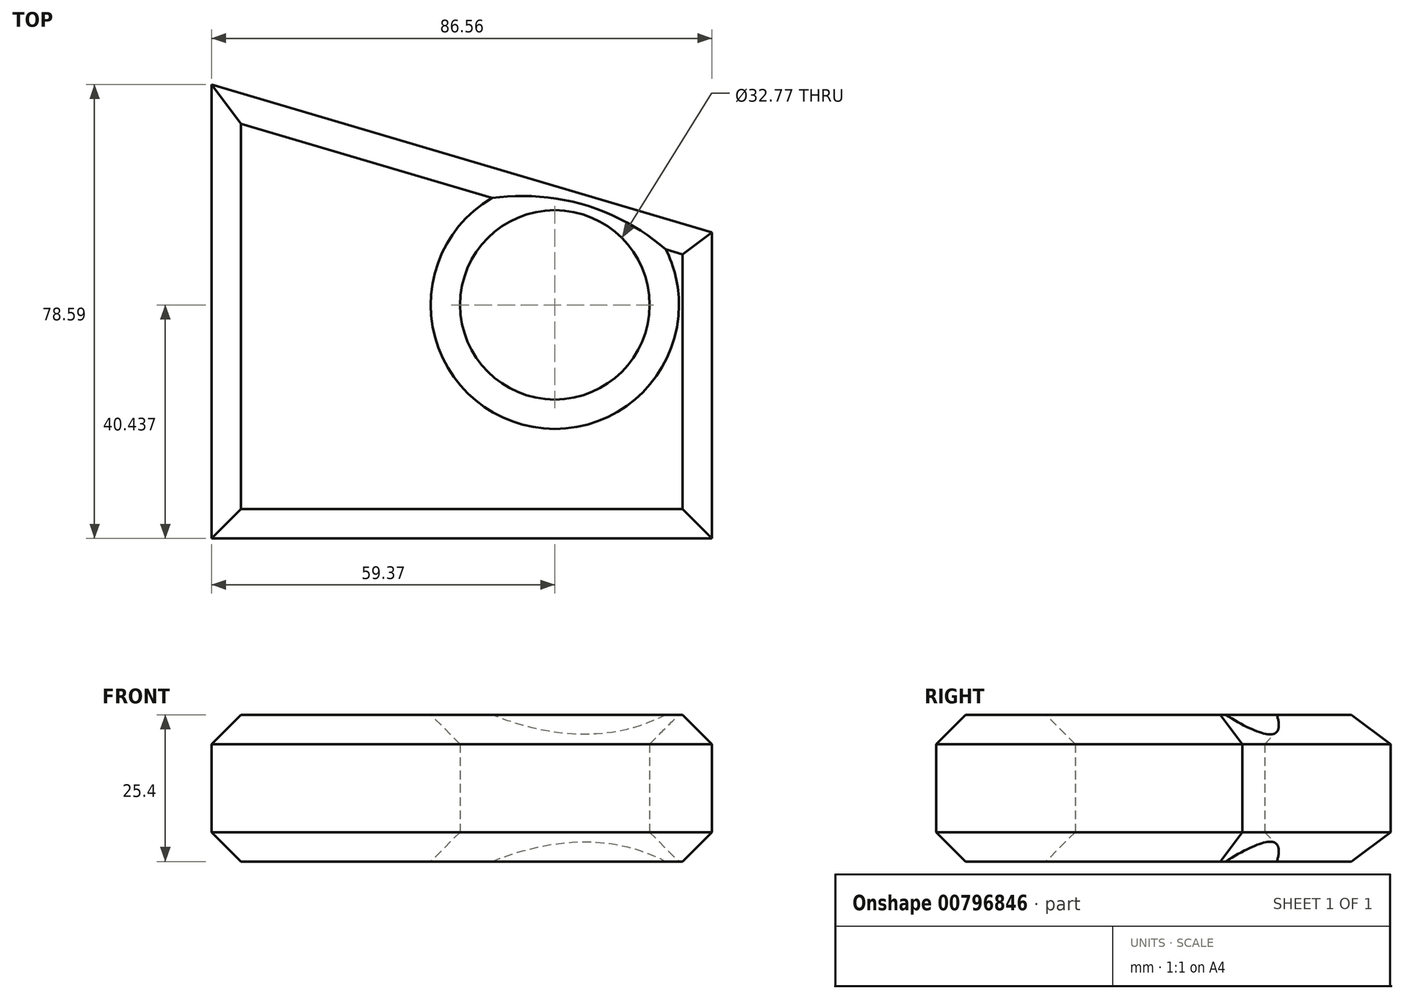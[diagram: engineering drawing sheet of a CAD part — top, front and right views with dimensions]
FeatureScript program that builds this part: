
annotation { "Feature Type Name" : "Feature", "Feature Type Description" : "" }
export const myFeature = defineFeature(function(context is Context, id is Id, definition is map)
    precondition{}
    {
        {
            var Q0;
            Q0=qCreatedBy(makeId("Top.planeOp"),FACE);
            var sketch = newSketch(context, id + "F0", { "sketchPlane" : qUnion([Q0])});
            skLineSegment(sketch, "E0", {"start": v(-59.37, 33.74) * mm, "end": v(-59.37, -44.85) * mm});
            skLineSegment(sketch, "E1", {"start": v(-59.37, -44.85) * mm, "end": v(27.2, -44.85) * mm});
            skLineSegment(sketch, "E2", {"start": v(27.2, -44.85) * mm, "end": v(27.2, 8.11) * mm});
            skLineSegment(sketch, "E3", {"start": v(27.2, 8.11) * mm, "end": v(-59.37, 33.74) * mm});
            skCircle(sketch, "E4", {"center": v(0, -4.41) * mm, "radius": 16.39 * mm});
            skSolve(sketch);
        }
        {
            var Q0;
            Q0=makeQuery(id+"F0.imprint","IMPRINT",FACE,{"disambiguationData":[TD([[makeQuery(id+"F0.imprint","IMPRINT",EDGE,{"derivedFrom":sQuery(id+"F0.wireOp",EDGE,"E0")}),1.0]])]});
            extrude(context, id + "F1", {"entities" : qUnion([Q0]), "depth" : 25.4 * mm, "offsetDistance" : 25.4 * mm});
        }
        {
            var Q0;
            Q0=makeQuery(id+"F1.opExtrude","CAP_FACE",FACE,{"disambiguationData":[OSD([sQuery(id+"F0.wireOp",EDGE,"E0"),sQuery(id+"F0.wireOp",EDGE,"E1"),sQuery(id+"F0.wireOp",EDGE,"E2"),sQuery(id+"F0.wireOp",EDGE,"E3"),sQuery(id+"F0.wireOp",EDGE,"E4")])],"isStart":false});
            chamfer(context, id + "F2", {"entities" : qUnion([Q0]), "width" : 5.08 * mm, "tangentPropagation" : true});
        }
        {
            var Q0;
            Q0=makeQuery(id+"F1.opExtrude","CAP_FACE",FACE,{"disambiguationData":[OSD([sQuery(id+"F0.wireOp",EDGE,"E0"),sQuery(id+"F0.wireOp",EDGE,"E1"),sQuery(id+"F0.wireOp",EDGE,"E2"),sQuery(id+"F0.wireOp",EDGE,"E3"),sQuery(id+"F0.wireOp",EDGE,"E4")])],"isStart":true});
            chamfer(context, id + "F3", {"entities" : qUnion([Q0]), "width" : 5.08 * mm, "tangentPropagation" : true});
        }
    });
